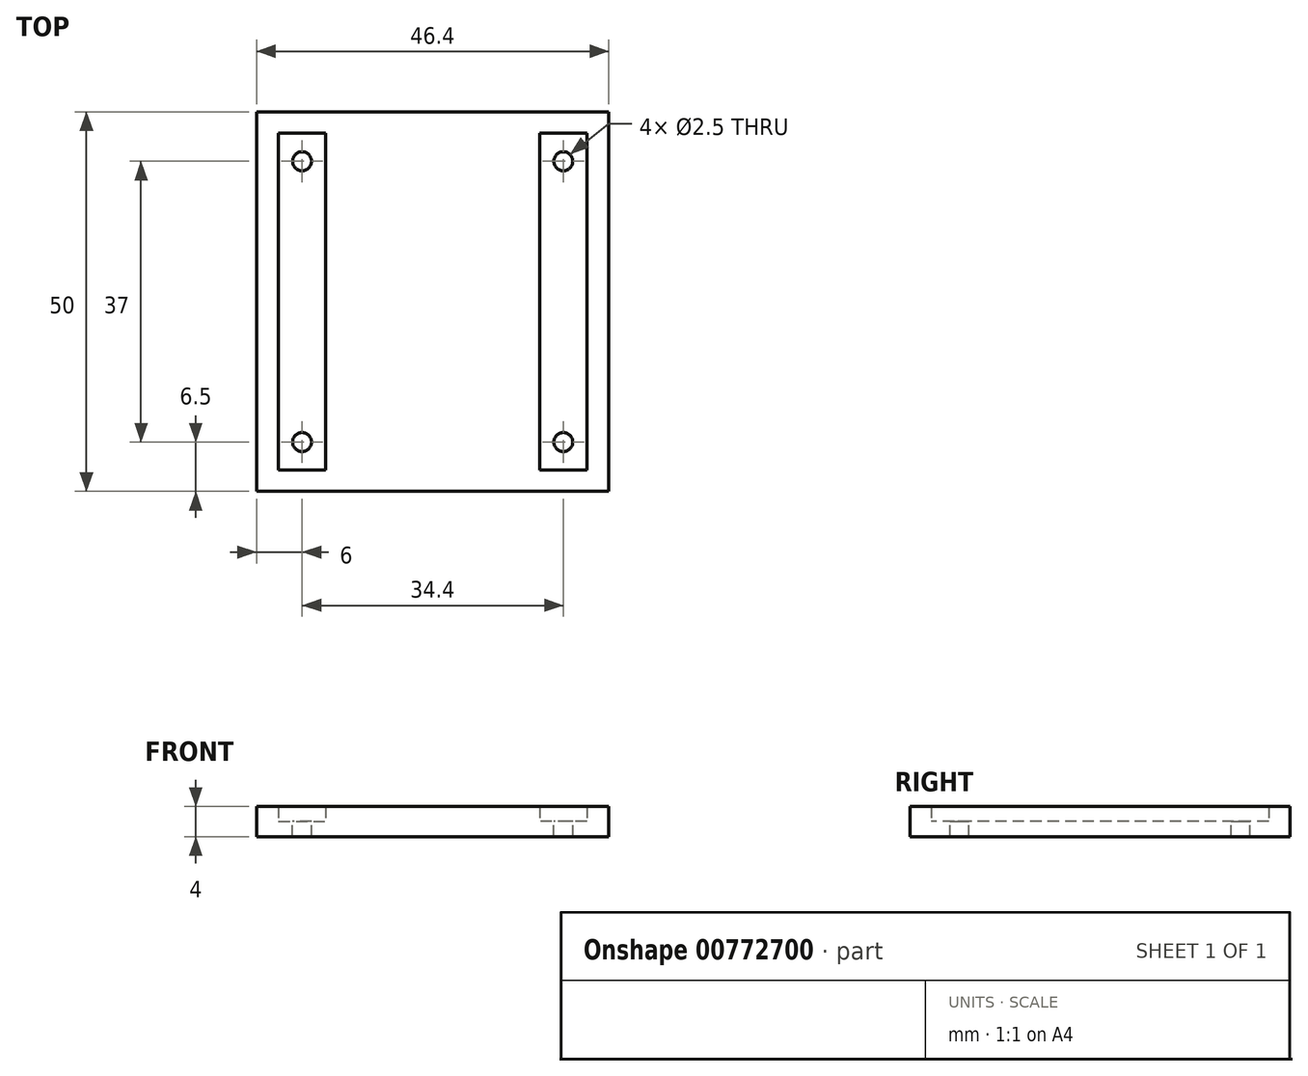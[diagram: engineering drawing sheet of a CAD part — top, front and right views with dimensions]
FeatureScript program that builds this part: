
annotation { "Feature Type Name" : "Feature", "Feature Type Description" : "" }
export const myFeature = defineFeature(function(context is Context, id is Id, definition is map)
    precondition{}
    {
        {
            var Q0;
            Q0=qCreatedBy(makeId("Top.planeOp"),FACE);
            var sketch = newSketch(context, id + "F0", { "sketchPlane" : qUnion([Q0])});
            skLineSegment(sketch, "E0.bottom", {"start": v(-23.2, 25) * mm, "end": v(23.2, 25) * mm});
            skLineSegment(sketch, "E0.top", {"start": v(-23.2, -25) * mm, "end": v(23.2, -25) * mm});
            skLineSegment(sketch, "E0.left", {"start": v(-23.2, 25) * mm, "end": v(-23.2, -25) * mm});
            skLineSegment(sketch, "E0.right", {"start": v(23.2, 25) * mm, "end": v(23.2, -25) * mm});
            skLineSegment(sketch, "E1.bottom", {"start": v(-20.3, 22.2) * mm, "end": v(-14.1, 22.2) * mm});
            skLineSegment(sketch, "E1.top", {"start": v(-20.3, -22.2) * mm, "end": v(-14.1, -22.2) * mm});
            skLineSegment(sketch, "E1.left", {"start": v(-20.3, 22.2) * mm, "end": v(-20.3, -22.2) * mm});
            skLineSegment(sketch, "E1.right", {"start": v(-14.1, 22.2) * mm, "end": v(-14.1, -22.2) * mm});
            skCircle(sketch, "E2", {"center": v(-17.2, 18.5) * mm, "radius": 1.25 * mm});
            skCircle(sketch, "E3", {"center": v(-17.2, -18.5) * mm, "radius": 1.25 * mm});
            skLineSegment(sketch, "E4", {"start": v(-17.2, 27.66) * mm, "end": v(-17.2, -38.97) * mm, "construction": true});
            skLineSegment(sketch, "E5.MirrorCS", {"start": v(20.3, -22.2) * mm, "end": v(14.1, -22.2) * mm});
            skCircle(sketch, "E6.MirrorC", {"center": v(17.2, -18.5) * mm, "radius": 1.25 * mm});
            skCircle(sketch, "E7.MirrorC", {"center": v(17.2, 18.5) * mm, "radius": 1.25 * mm});
            skLineSegment(sketch, "E8.MirrorCS", {"start": v(14.1, 22.2) * mm, "end": v(14.1, -22.2) * mm});
            skLineSegment(sketch, "E9.MirrorCS", {"start": v(20.3, 22.2) * mm, "end": v(20.3, -22.2) * mm});
            skLineSegment(sketch, "E10.MirrorCS", {"start": v(20.3, 22.2) * mm, "end": v(14.1, 22.2) * mm});
            skSolve(sketch);
        }
        {
            var Q0;
            Q0=makeQuery(id+"F0.imprint","IMPRINT",FACE,{"disambiguationData":[TD([[makeQuery(id+"F0.imprint","IMPRINT",EDGE,{"derivedFrom":sQuery(id+"F0.wireOp",EDGE,"E0.bottom")}),-1.0]])]});
            var Q1;
            Q1=makeQuery(id+"F0.imprint","IMPRINT",FACE,{"disambiguationData":[TD([[makeQuery(id+"F0.imprint","IMPRINT",EDGE,{"derivedFrom":sQuery(id+"F0.wireOp",EDGE,"E1.bottom")}),-1.0]])]});
            var Q2;
            Q2=makeQuery(id+"F0.imprint","IMPRINT",FACE,{"disambiguationData":[TD([[makeQuery(id+"F0.imprint","IMPRINT",EDGE,{"derivedFrom":sQuery(id+"F0.wireOp",EDGE,"E5.MirrorCS")}),-1.0]])]});
            extrude(context, id + "F1", {"entities" : qUnion([Q0, Q1, Q2]), "oppositeDirection" : true, "depth" : 2 * mm, "offsetDistance" : 25 * mm});
        }
        {
            var Q0;
            Q0=makeQuery(id+"F0.imprint","IMPRINT",FACE,{"disambiguationData":[TD([[makeQuery(id+"F0.imprint","IMPRINT",EDGE,{"derivedFrom":sQuery(id+"F0.wireOp",EDGE,"E0.bottom")}),-1.0]])]});
            extrude(context, id + "F2", {"entities" : qUnion([Q0]), "operationType" : NewBodyOperationType.ADD, "depth" : 2 * mm, "offsetDistance" : 25 * mm});
        }
    });
